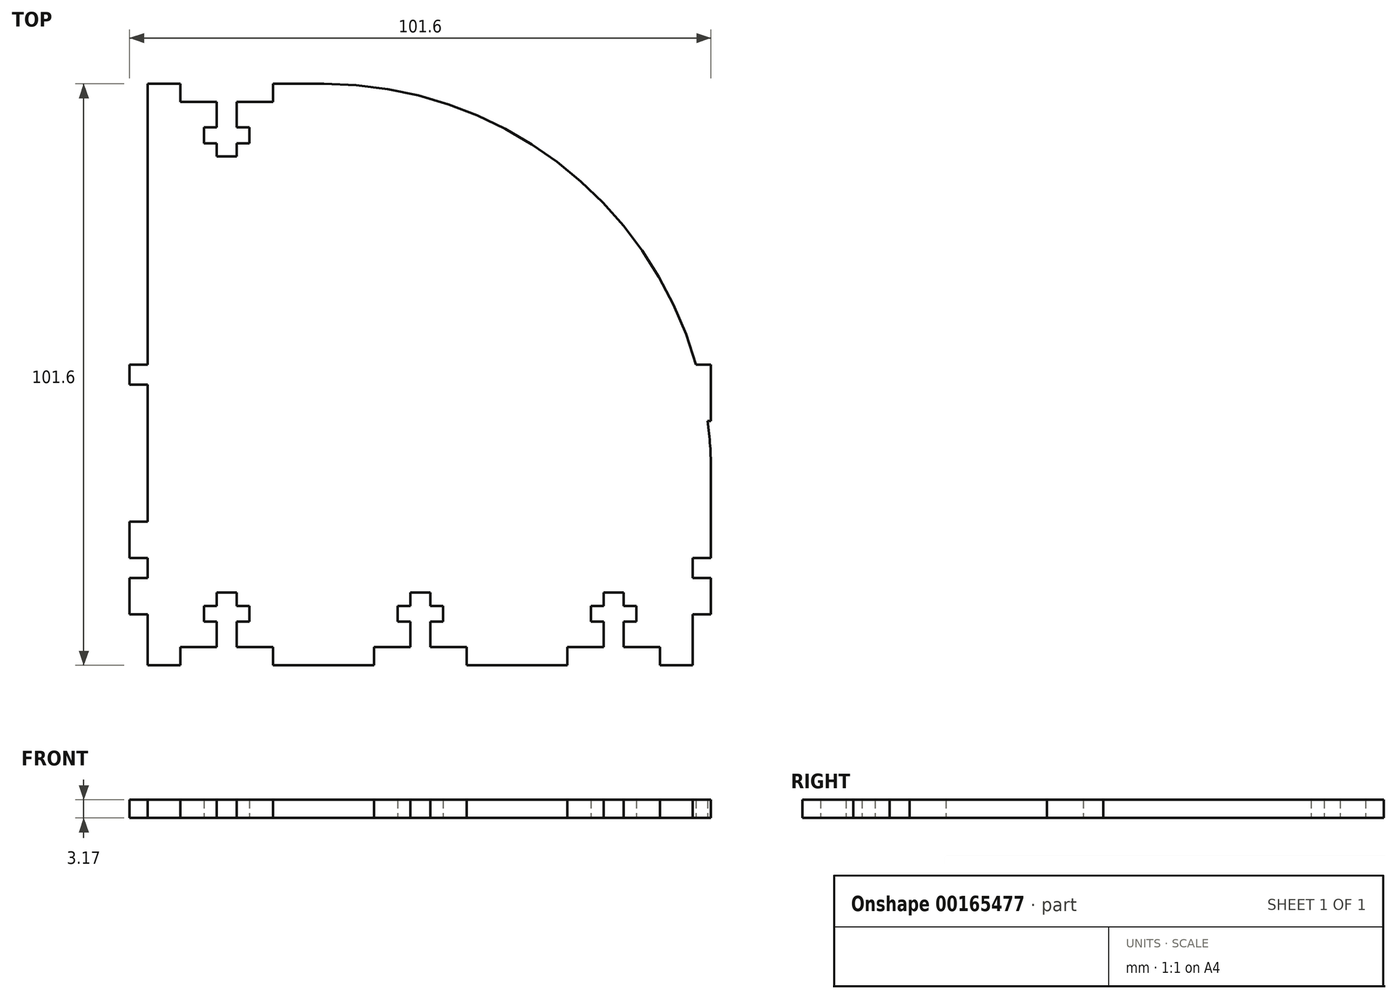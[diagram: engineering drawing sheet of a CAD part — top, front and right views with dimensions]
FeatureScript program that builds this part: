
annotation { "Feature Type Name" : "Feature", "Feature Type Description" : "" }
export const myFeature = defineFeature(function(context is Context, id is Id, definition is map)
    precondition{}
    {
        {
            var Q0;
            Q0=qCreatedBy(makeId("Top.planeOp"),FACE);
            var sketch = newSketch(context, id + "F0", { "sketchPlane" : qUnion([Q0])});
            skLineSegment(sketch, "E0.top", {"start": v(-48.14, 94.54) * mm, "end": v(53.46, 94.54) * mm});
            skLineSegment(sketch, "E0.left", {"start": v(-48.14, -7.06) * mm, "end": v(-48.14, 94.54) * mm});
            skLineSegment(sketch, "E0.right", {"start": v(53.46, -7.06) * mm, "end": v(53.46, 94.54) * mm});
            skLineSegment(sketch, "E1.bottom", {"start": v(-32.9, 94.54) * mm, "end": v(-29.4, 94.54) * mm});
            skLineSegment(sketch, "E1.top", {"start": v(-32.9, 81.84) * mm, "end": v(-29.4, 81.84) * mm});
            skLineSegment(sketch, "E1.left", {"start": v(-32.9, 94.54) * mm, "end": v(-32.9, 81.84) * mm});
            skLineSegment(sketch, "E1.right", {"start": v(-29.4, 94.54) * mm, "end": v(-29.4, 81.84) * mm});
            skLineSegment(sketch, "E2.bottom", {"start": v(-27.18, 84.14) * mm, "end": v(-35.11, 84.14) * mm});
            skLineSegment(sketch, "E2.top", {"start": v(-27.18, 86.92) * mm, "end": v(-35.11, 86.92) * mm});
            skLineSegment(sketch, "E2.left", {"start": v(-27.18, 84.14) * mm, "end": v(-27.18, 86.92) * mm});
            skLineSegment(sketch, "E2.right", {"start": v(-35.11, 84.14) * mm, "end": v(-35.11, 86.92) * mm});
            skLineSegment(sketch, "E3", {"start": v(-108, 43.74) * mm, "end": v(92.5, 43.74) * mm});
            skLineSegment(sketch, "E4.bottom", {"start": v(-39.25, 94.54) * mm, "end": v(-23.04, 94.54) * mm});
            skLineSegment(sketch, "E4.top", {"start": v(-39.25, 91.37) * mm, "end": v(-23.04, 91.37) * mm});
            skLineSegment(sketch, "E4.left", {"start": v(-39.25, 94.54) * mm, "end": v(-39.25, 91.37) * mm});
            skLineSegment(sketch, "E4.right", {"start": v(-23.04, 94.54) * mm, "end": v(-23.04, 91.37) * mm});
            skLineSegment(sketch, "E5.1.0.0", {"start": v(-5.44, 91.37) * mm, "end": v(10.76, 91.37) * mm});
            skLineSegment(sketch, "E5.1.0.1", {"start": v(4.41, 94.54) * mm, "end": v(4.41, 81.84) * mm});
            skLineSegment(sketch, "E5.1.0.2", {"start": v(0.9, 94.54) * mm, "end": v(0.9, 81.84) * mm});
            skLineSegment(sketch, "E5.1.0.3", {"start": v(-5.44, 94.54) * mm, "end": v(10.76, 94.54) * mm});
            skLineSegment(sketch, "E5.1.0.4", {"start": v(6.63, 86.92) * mm, "end": v(-1.3, 86.92) * mm});
            skLineSegment(sketch, "E5.1.0.6", {"start": v(-5.44, 94.54) * mm, "end": v(-5.44, 91.37) * mm});
            skLineSegment(sketch, "E5.1.0.7", {"start": v(0.9, 94.54) * mm, "end": v(4.41, 94.54) * mm});
            skLineSegment(sketch, "E5.1.0.8", {"start": v(10.76, 94.54) * mm, "end": v(10.76, 91.37) * mm});
            skLineSegment(sketch, "E5.1.0.9", {"start": v(0.9, 81.84) * mm, "end": v(4.41, 81.84) * mm});
            skLineSegment(sketch, "E5.1.0.10", {"start": v(6.63, 84.14) * mm, "end": v(6.63, 86.92) * mm});
            skLineSegment(sketch, "E5.1.0.11", {"start": v(6.63, 84.14) * mm, "end": v(-1.3, 84.14) * mm});
            skLineSegment(sketch, "E5.1.0.12", {"start": v(-1.3, 84.14) * mm, "end": v(-1.3, 86.92) * mm});
            skLineSegment(sketch, "E5.2.0.0", {"start": v(28.37, 91.37) * mm, "end": v(44.57, 91.37) * mm});
            skLineSegment(sketch, "E5.2.0.1", {"start": v(38.22, 94.54) * mm, "end": v(38.22, 81.84) * mm});
            skLineSegment(sketch, "E5.2.0.2", {"start": v(34.72, 94.54) * mm, "end": v(34.72, 81.84) * mm});
            skLineSegment(sketch, "E5.2.0.3", {"start": v(28.37, 94.54) * mm, "end": v(44.57, 94.54) * mm});
            skLineSegment(sketch, "E5.2.0.4", {"start": v(40.44, 86.92) * mm, "end": v(32.5, 86.92) * mm});
            skLineSegment(sketch, "E5.2.0.6", {"start": v(28.37, 94.54) * mm, "end": v(28.37, 91.37) * mm});
            skLineSegment(sketch, "E5.2.0.7", {"start": v(34.72, 94.54) * mm, "end": v(38.22, 94.54) * mm});
            skLineSegment(sketch, "E5.2.0.8", {"start": v(44.57, 94.54) * mm, "end": v(44.57, 91.37) * mm});
            skLineSegment(sketch, "E5.2.0.9", {"start": v(34.72, 81.84) * mm, "end": v(38.22, 81.84) * mm});
            skLineSegment(sketch, "E5.2.0.10", {"start": v(40.44, 84.14) * mm, "end": v(40.44, 86.92) * mm});
            skLineSegment(sketch, "E5.2.0.11", {"start": v(40.44, 84.14) * mm, "end": v(32.5, 84.14) * mm});
            skLineSegment(sketch, "E5.2.0.12", {"start": v(32.5, 84.14) * mm, "end": v(32.5, 86.92) * mm});
            skLineSegment(sketch, "E5.direction1", {"start": v(-32.9, 81.84) * mm, "end": v(0.9, 81.84) * mm, "construction": true});
            skLineSegment(sketch, "E6.MirrorCS", {"start": v(0.9, 5.64) * mm, "end": v(4.41, 5.64) * mm});
            skLineSegment(sketch, "E7.MirrorCS", {"start": v(-32.9, 5.64) * mm, "end": v(-29.4, 5.64) * mm});
            skLineSegment(sketch, "E8.MirrorCS", {"start": v(-23.04, -7.06) * mm, "end": v(-23.04, -3.88) * mm});
            skLineSegment(sketch, "E9.MirrorCS", {"start": v(-32.9, -7.06) * mm, "end": v(-29.4, -7.06) * mm});
            skLineSegment(sketch, "E10.MirrorCS", {"start": v(-35.11, 3.34) * mm, "end": v(-35.11, 0.56) * mm});
            skLineSegment(sketch, "E11.MirrorCS", {"start": v(-5.44, -7.06) * mm, "end": v(-5.44, -3.88) * mm});
            skLineSegment(sketch, "E12.MirrorCS", {"start": v(0.9, -7.06) * mm, "end": v(0.9, 5.64) * mm});
            skLineSegment(sketch, "E13.MirrorCS", {"start": v(-27.18, 3.34) * mm, "end": v(-27.18, 0.56) * mm});
            skLineSegment(sketch, "E14.MirrorCS", {"start": v(34.72, -7.06) * mm, "end": v(34.72, 5.64) * mm});
            skLineSegment(sketch, "E15.MirrorCS", {"start": v(0.9, -7.06) * mm, "end": v(4.41, -7.06) * mm});
            skLineSegment(sketch, "E16.MirrorCS", {"start": v(4.41, -7.06) * mm, "end": v(4.41, 5.64) * mm});
            skLineSegment(sketch, "E17.MirrorCS", {"start": v(40.44, 3.34) * mm, "end": v(40.44, 0.56) * mm});
            skLineSegment(sketch, "E18.MirrorCS", {"start": v(-39.25, -7.06) * mm, "end": v(-23.04, -7.06) * mm});
            skLineSegment(sketch, "E19.MirrorCS", {"start": v(-1.3, 3.34) * mm, "end": v(-1.3, 0.56) * mm});
            skLineSegment(sketch, "E20.MirrorCS", {"start": v(-5.44, -7.06) * mm, "end": v(10.76, -7.06) * mm});
            skLineSegment(sketch, "E21.MirrorCS", {"start": v(34.72, 5.64) * mm, "end": v(38.22, 5.64) * mm});
            skLineSegment(sketch, "E22.MirrorCS", {"start": v(28.37, -7.06) * mm, "end": v(28.37, -3.88) * mm});
            skLineSegment(sketch, "E23.MirrorCS", {"start": v(40.44, 3.34) * mm, "end": v(32.5, 3.34) * mm});
            skLineSegment(sketch, "E24.MirrorCS", {"start": v(28.37, -7.06) * mm, "end": v(44.57, -7.06) * mm});
            skLineSegment(sketch, "E25.MirrorCS", {"start": v(6.63, 3.34) * mm, "end": v(6.63, 0.56) * mm});
            skLineSegment(sketch, "E26.MirrorCS", {"start": v(10.76, -7.06) * mm, "end": v(10.76, -3.88) * mm});
            skLineSegment(sketch, "E27.MirrorCS", {"start": v(-32.9, -7.06) * mm, "end": v(-32.9, 5.64) * mm});
            skLineSegment(sketch, "E28.MirrorCS", {"start": v(-27.18, 3.34) * mm, "end": v(-35.11, 3.34) * mm});
            skLineSegment(sketch, "E29.MirrorCS", {"start": v(34.72, -7.06) * mm, "end": v(38.22, -7.06) * mm});
            skLineSegment(sketch, "E30.MirrorCS", {"start": v(44.57, -7.06) * mm, "end": v(44.57, -3.88) * mm});
            skLineSegment(sketch, "E31.MirrorCS", {"start": v(-39.25, -7.06) * mm, "end": v(-39.25, -3.88) * mm});
            skLineSegment(sketch, "E32.MirrorCS", {"start": v(32.5, 3.34) * mm, "end": v(32.5, 0.56) * mm});
            skLineSegment(sketch, "E33.MirrorCS", {"start": v(6.63, 3.34) * mm, "end": v(-1.3, 3.34) * mm});
            skLineSegment(sketch, "E34.MirrorCS", {"start": v(-29.4, -7.06) * mm, "end": v(-29.4, 5.64) * mm});
            skLineSegment(sketch, "E35.MirrorCS", {"start": v(38.22, -7.06) * mm, "end": v(38.22, 5.64) * mm});
            skLineSegment(sketch, "E36.MirrorCS", {"start": v(40.44, 0.56) * mm, "end": v(32.5, 0.56) * mm});
            skLineSegment(sketch, "E37.MirrorCS", {"start": v(-27.18, 0.56) * mm, "end": v(-35.11, 0.56) * mm});
            skLineSegment(sketch, "E38.MirrorCS", {"start": v(-32.9, 5.64) * mm, "end": v(0.9, 5.64) * mm, "construction": true});
            skLineSegment(sketch, "E39.MirrorCS", {"start": v(28.37, -3.88) * mm, "end": v(44.57, -3.88) * mm});
            skLineSegment(sketch, "E40.MirrorCS", {"start": v(-39.25, -3.88) * mm, "end": v(-23.04, -3.88) * mm});
            skLineSegment(sketch, "E41.MirrorCS", {"start": v(6.63, 0.56) * mm, "end": v(-1.3, 0.56) * mm});
            skLineSegment(sketch, "E42.MirrorCS", {"start": v(53.46, 94.54) * mm, "end": v(53.46, -7.06) * mm});
            skLineSegment(sketch, "E43.MirrorCS", {"start": v(-5.44, -3.88) * mm, "end": v(10.76, -3.88) * mm});
            skLineSegment(sketch, "E44.MirrorCS", {"start": v(-48.14, -7.06) * mm, "end": v(53.46, -7.06) * mm});
            skLineSegment(sketch, "E45.MirrorCS", {"start": v(-48.14, 94.54) * mm, "end": v(-48.14, -7.06) * mm});
            skLineSegment(sketch, "E46.bottom", {"start": v(-48.14, 94.54) * mm, "end": v(-44.96, 94.54) * mm});
            skLineSegment(sketch, "E46.top", {"start": v(-48.14, -7.06) * mm, "end": v(-44.96, -7.06) * mm});
            skLineSegment(sketch, "E46.right", {"start": v(-44.96, 94.54) * mm, "end": v(-44.96, -7.06) * mm});
            skLineSegment(sketch, "E47.bottom", {"start": v(53.46, -7.06) * mm, "end": v(50.29, -7.06) * mm});
            skLineSegment(sketch, "E47.top", {"start": v(53.46, 94.54) * mm, "end": v(50.29, 94.54) * mm});
            skLineSegment(sketch, "E47.right", {"start": v(50.29, -7.06) * mm, "end": v(50.29, 94.54) * mm});
            skLineSegment(sketch, "E48.bottom", {"start": v(-44.96, 1.83) * mm, "end": v(-48.14, 1.83) * mm});
            skLineSegment(sketch, "E48.top", {"start": v(-44.96, 8.18) * mm, "end": v(-48.14, 8.18) * mm});
            skLineSegment(sketch, "E48.left", {"start": v(-44.96, 1.83) * mm, "end": v(-44.96, 8.18) * mm});
            skLineSegment(sketch, "E48.right", {"start": v(-48.14, 1.83) * mm, "end": v(-48.14, 8.18) * mm});
            skLineSegment(sketch, "E49.top", {"start": v(-44.96, 11.69) * mm, "end": v(-48.14, 11.69) * mm});
            skLineSegment(sketch, "E49.left", {"start": v(-44.96, 8.18) * mm, "end": v(-44.96, 11.69) * mm});
            skLineSegment(sketch, "E49.right", {"start": v(-48.14, 8.18) * mm, "end": v(-48.14, 11.69) * mm});
            skLineSegment(sketch, "E50.top", {"start": v(-44.96, 18.04) * mm, "end": v(-48.14, 18.04) * mm});
            skLineSegment(sketch, "E50.left", {"start": v(-44.96, 11.69) * mm, "end": v(-44.96, 18.04) * mm});
            skLineSegment(sketch, "E50.right", {"start": v(-48.14, 11.69) * mm, "end": v(-48.14, 18.04) * mm});
            skLineSegment(sketch, "E51.0.1.0", {"start": v(-48.14, 41.99) * mm, "end": v(-48.14, 45.5) * mm});
            skLineSegment(sketch, "E51.0.1.1", {"start": v(-44.96, 35.64) * mm, "end": v(-44.96, 41.99) * mm});
            skLineSegment(sketch, "E51.0.1.2", {"start": v(-44.96, 35.64) * mm, "end": v(-48.14, 35.64) * mm});
            skLineSegment(sketch, "E51.0.1.3", {"start": v(-48.14, 45.5) * mm, "end": v(-48.14, 51.84) * mm});
            skLineSegment(sketch, "E51.0.1.4", {"start": v(-44.96, 41.99) * mm, "end": v(-44.96, 45.5) * mm});
            skLineSegment(sketch, "E51.0.1.5", {"start": v(-44.96, 45.5) * mm, "end": v(-48.14, 45.5) * mm});
            skLineSegment(sketch, "E51.0.1.6", {"start": v(-44.96, 45.5) * mm, "end": v(-44.96, 51.84) * mm});
            skLineSegment(sketch, "E51.0.1.7", {"start": v(-48.14, 35.64) * mm, "end": v(-48.14, 41.99) * mm});
            skLineSegment(sketch, "E51.0.1.8", {"start": v(-44.96, 41.99) * mm, "end": v(-48.14, 41.99) * mm});
            skLineSegment(sketch, "E51.0.1.9", {"start": v(-44.96, 51.84) * mm, "end": v(-48.14, 51.84) * mm});
            skLineSegment(sketch, "E51.0.1.10", {"start": v(-44.96, 41.99) * mm, "end": v(-48.14, 41.99) * mm});
            skLineSegment(sketch, "E51.0.1.11", {"start": v(-44.96, 45.5) * mm, "end": v(-48.14, 45.5) * mm});
            skLineSegment(sketch, "E51.0.2.0", {"start": v(-48.14, 75.8) * mm, "end": v(-48.14, 79.3) * mm});
            skLineSegment(sketch, "E51.0.2.1", {"start": v(-44.96, 69.45) * mm, "end": v(-44.96, 75.8) * mm});
            skLineSegment(sketch, "E51.0.2.2", {"start": v(-44.96, 69.45) * mm, "end": v(-48.14, 69.45) * mm});
            skLineSegment(sketch, "E51.0.2.3", {"start": v(-48.14, 79.3) * mm, "end": v(-48.14, 85.65) * mm});
            skLineSegment(sketch, "E51.0.2.4", {"start": v(-44.96, 75.8) * mm, "end": v(-44.96, 79.3) * mm});
            skLineSegment(sketch, "E51.0.2.5", {"start": v(-44.96, 79.3) * mm, "end": v(-48.14, 79.3) * mm});
            skLineSegment(sketch, "E51.0.2.6", {"start": v(-44.96, 79.3) * mm, "end": v(-44.96, 85.65) * mm});
            skLineSegment(sketch, "E51.0.2.7", {"start": v(-48.14, 69.45) * mm, "end": v(-48.14, 75.8) * mm});
            skLineSegment(sketch, "E51.0.2.8", {"start": v(-44.96, 75.8) * mm, "end": v(-48.14, 75.8) * mm});
            skLineSegment(sketch, "E51.0.2.9", {"start": v(-44.96, 85.65) * mm, "end": v(-48.14, 85.65) * mm});
            skLineSegment(sketch, "E51.0.2.10", {"start": v(-44.96, 75.8) * mm, "end": v(-48.14, 75.8) * mm});
            skLineSegment(sketch, "E51.0.2.11", {"start": v(-44.96, 79.3) * mm, "end": v(-48.14, 79.3) * mm});
            skLineSegment(sketch, "E51.direction1", {"start": v(-48.14, 1.83) * mm, "end": v(-22.74, 1.83) * mm, "construction": true});
            skLineSegment(sketch, "E51.direction2", {"start": v(-48.14, 1.83) * mm, "end": v(-48.14, 35.64) * mm, "construction": true});
            skLineSegment(sketch, "E52", {"start": v(2.66, 112.42) * mm, "end": v(2.66, 100.35) * mm});
            skLineSegment(sketch, "E53.MirrorCS", {"start": v(50.29, 75.8) * mm, "end": v(53.46, 75.8) * mm});
            skLineSegment(sketch, "E54.MirrorCS", {"start": v(50.29, 11.69) * mm, "end": v(53.46, 11.69) * mm});
            skLineSegment(sketch, "E55.MirrorCS", {"start": v(50.29, 79.3) * mm, "end": v(53.46, 79.3) * mm});
            skLineSegment(sketch, "E56.MirrorCS", {"start": v(50.29, 8.18) * mm, "end": v(53.46, 8.18) * mm});
            skLineSegment(sketch, "E57.MirrorCS", {"start": v(50.29, 45.5) * mm, "end": v(53.46, 45.5) * mm});
            skLineSegment(sketch, "E58.MirrorCS", {"start": v(50.29, 41.99) * mm, "end": v(53.46, 41.99) * mm});
            skLineSegment(sketch, "E59.MirrorCS", {"start": v(53.46, 75.8) * mm, "end": v(53.46, 79.3) * mm});
            skLineSegment(sketch, "E60.MirrorCS", {"start": v(53.46, 8.18) * mm, "end": v(53.46, 11.69) * mm});
            skLineSegment(sketch, "E61.MirrorCS", {"start": v(50.29, 41.99) * mm, "end": v(50.29, 45.5) * mm});
            skLineSegment(sketch, "E62.MirrorCS", {"start": v(50.29, 1.83) * mm, "end": v(53.46, 1.83) * mm});
            skLineSegment(sketch, "E63.MirrorCS", {"start": v(50.29, 8.18) * mm, "end": v(50.29, 11.69) * mm});
            skLineSegment(sketch, "E64.MirrorCS", {"start": v(53.46, 41.99) * mm, "end": v(53.46, 45.5) * mm});
            skLineSegment(sketch, "E65.MirrorCS", {"start": v(53.46, 1.83) * mm, "end": v(53.46, 8.18) * mm});
            skLineSegment(sketch, "E66.MirrorCS", {"start": v(50.29, 75.8) * mm, "end": v(50.29, 79.3) * mm});
            skLineSegment(sketch, "E67.MirrorCS", {"start": v(50.29, 35.64) * mm, "end": v(53.46, 35.64) * mm});
            skLineSegment(sketch, "E68.MirrorCS", {"start": v(53.46, 35.64) * mm, "end": v(53.46, 41.99) * mm});
            skLineSegment(sketch, "E69.MirrorCS", {"start": v(50.29, 18.04) * mm, "end": v(53.46, 18.04) * mm});
            skLineSegment(sketch, "E70.MirrorCS", {"start": v(50.29, 69.45) * mm, "end": v(50.29, 75.8) * mm});
            skLineSegment(sketch, "E71.MirrorCS", {"start": v(50.29, 11.69) * mm, "end": v(50.29, 18.04) * mm});
            skLineSegment(sketch, "E72.MirrorCS", {"start": v(53.46, 45.5) * mm, "end": v(53.46, 51.84) * mm});
            skLineSegment(sketch, "E73.MirrorCS", {"start": v(53.46, 69.45) * mm, "end": v(53.46, 75.8) * mm});
            skLineSegment(sketch, "E74.MirrorCS", {"start": v(50.29, 79.3) * mm, "end": v(50.29, 85.65) * mm});
            skLineSegment(sketch, "E75.MirrorCS", {"start": v(50.29, 69.45) * mm, "end": v(53.46, 69.45) * mm});
            skLineSegment(sketch, "E76.MirrorCS", {"start": v(50.29, 35.64) * mm, "end": v(50.29, 41.99) * mm});
            skLineSegment(sketch, "E77.MirrorCS", {"start": v(50.29, 51.84) * mm, "end": v(53.46, 51.84) * mm});
            skLineSegment(sketch, "E78.MirrorCS", {"start": v(50.29, 1.83) * mm, "end": v(50.29, 8.18) * mm});
            skLineSegment(sketch, "E79.MirrorCS", {"start": v(50.29, 45.5) * mm, "end": v(50.29, 51.84) * mm});
            skLineSegment(sketch, "E80.MirrorCS", {"start": v(53.46, 11.69) * mm, "end": v(53.46, 18.04) * mm});
            skLineSegment(sketch, "E81.MirrorCS", {"start": v(53.46, 79.3) * mm, "end": v(53.46, 85.65) * mm});
            skLineSegment(sketch, "E82.MirrorCS", {"start": v(50.29, 85.65) * mm, "end": v(53.46, 85.65) * mm});
            skLineSegment(sketch, "E83.MirrorCS", {"start": v(53.46, 1.83) * mm, "end": v(53.46, 35.64) * mm, "construction": true});
            skLineSegment(sketch, "E84.MirrorCS", {"start": v(50.29, 94.54) * mm, "end": v(50.29, -7.06) * mm});
            skArc(sketch, "E85", {"start": v(53.46, 26.93) * mm, "mid": v(33.66, 74.74) * mm, "end": v(-14.15, 94.54) * mm});
            skLineSegment(sketch, "E86.bottom", {"start": v(53.46, 26.93) * mm, "end": v(50.29, 26.93) * mm});
            skLineSegment(sketch, "E86.top", {"start": v(53.46, 18.04) * mm, "end": v(50.29, 18.04) * mm});
            skLineSegment(sketch, "E86.left", {"start": v(53.46, 26.93) * mm, "end": v(53.46, 18.04) * mm});
            skLineSegment(sketch, "E86.right", {"start": v(50.29, 26.93) * mm, "end": v(50.29, 18.04) * mm});
            skSolve(sketch);
        }
        {
            var Q0;
            {var subQ0=sQuery(id+"F0.wireOp",EDGE,"E84.MirrorCS");var subQ1=sQuery(id+"F0.wireOp",EDGE,"E58.MirrorCS");var subQ2=makeQuery(id+"F0.imprint","INTERSECT",VERTEX,{"derivedFrom":[subQ1,subQ0]});Q0=makeQuery(id+"F0.imprint","IMPRINT",FACE,{"disambiguationData":[TD([[makeQuery(id+"F0.imprint","IMPRINT",EDGE,{"disambiguationData":[TD([[subQ2,-1.0]])],"derivedFrom":subQ1}),-1.0]])]});}
            var Q1;
            {var subQ31=sQuery(id+"F0.wireOp",EDGE,"E1.top");Q1=makeQuery(id+"F0.imprint","IMPRINT",FACE,{"disambiguationData":[TD([[makeQuery(id+"F0.imprint","IMPRINT",EDGE,{"derivedFrom":subQ31}),-1.0]])]});}
            var Q2;
            {var subQ50=sQuery(id+"F0.wireOp",EDGE,"E6.MirrorCS");Q2=makeQuery(id+"F0.imprint","IMPRINT",FACE,{"disambiguationData":[TD([[makeQuery(id+"F0.imprint","IMPRINT",EDGE,{"derivedFrom":subQ50}),1.0]])]});}
            var Q3;
            Q3=makeQuery(id+"F0.imprint","IMPRINT",FACE,{"disambiguationData":[TD([[makeQuery(id+"F0.imprint","IMPRINT",EDGE,{"derivedFrom":sQuery(id+"F0.wireOp",EDGE,"E51.0.1.3")}),-1.0]])]});
            var Q4;
            Q4=makeQuery(id+"F0.imprint","IMPRINT",FACE,{"disambiguationData":[TD([[makeQuery(id+"F0.imprint","IMPRINT",EDGE,{"derivedFrom":sQuery(id+"F0.wireOp",EDGE,"E51.0.2.1")}),1.0]])]});
            var Q5;
            Q5=makeQuery(id+"F0.imprint","IMPRINT",FACE,{"disambiguationData":[TD([[makeQuery(id+"F0.imprint","IMPRINT",EDGE,{"derivedFrom":sQuery(id+"F0.wireOp",EDGE,"E51.0.2.3")}),-1.0]])]});
            var Q6;
            Q6=makeQuery(id+"F0.imprint","IMPRINT",FACE,{"disambiguationData":[TD([[makeQuery(id+"F0.imprint","IMPRINT",EDGE,{"derivedFrom":sQuery(id+"F0.wireOp",EDGE,"E51.0.1.1")}),1.0]])]});
            var Q7;
            Q7=makeQuery(id+"F0.imprint","IMPRINT",FACE,{"disambiguationData":[TD([[makeQuery(id+"F0.imprint","IMPRINT",EDGE,{"derivedFrom":sQuery(id+"F0.wireOp",EDGE,"E49.top")}),-1.0]])]});
            var Q8;
            Q8=makeQuery(id+"F0.imprint","IMPRINT",FACE,{"disambiguationData":[TD([[makeQuery(id+"F0.imprint","IMPRINT",EDGE,{"derivedFrom":sQuery(id+"F0.wireOp",EDGE,"E48.bottom")}),-1.0]])]});
            var Q9;
            {var subQ0=sQuery(id+"F0.wireOp",EDGE,"E62.MirrorCS");Q9=makeQuery(id+"F0.imprint","IMPRINT",FACE,{"disambiguationData":[TD([[makeQuery(id+"F0.imprint","IMPRINT",EDGE,{"derivedFrom":subQ0}),1.0]])]});}
            var Q10;
            {var subQ0=sQuery(id+"F0.wireOp",EDGE,"E54.MirrorCS");Q10=makeQuery(id+"F0.imprint","IMPRINT",FACE,{"disambiguationData":[TD([[makeQuery(id+"F0.imprint","IMPRINT",EDGE,{"derivedFrom":subQ0}),1.0]])]});}
            var Q11;
            {var subQ0=sQuery(id+"F0.wireOp",EDGE,"E84.MirrorCS");var subQ1=sQuery(id+"F0.wireOp",EDGE,"E57.MirrorCS");var subQ2=makeQuery(id+"F0.imprint","INTERSECT",VERTEX,{"derivedFrom":[subQ1,subQ0]});Q11=makeQuery(id+"F0.imprint","IMPRINT",FACE,{"disambiguationData":[TD([[makeQuery(id+"F0.imprint","IMPRINT",EDGE,{"disambiguationData":[TD([[subQ2,-1.0]])],"derivedFrom":subQ1}),1.0]])]});}
            var Q12;
            {var subQ0=sQuery(id+"F0.wireOp",EDGE,"E5.1.0.6");var subQ1=sQuery(id+"F0.wireOp",EDGE,"E5.1.0.0");var subQ2=makeQuery(id+"F0.imprint","INTERSECT",VERTEX,{"derivedFrom":[subQ1,subQ0]});Q12=makeQuery(id+"F0.imprint","IMPRINT",FACE,{"disambiguationData":[TD([[makeQuery(id+"F0.imprint","IMPRINT",EDGE,{"disambiguationData":[TD([[subQ2,-1.0]])],"derivedFrom":subQ1}),1.0]])]});}
            var Q13;
            {var subQ0=sQuery(id+"F0.wireOp",EDGE,"E5.1.0.2");var subQ1=sQuery(id+"F0.wireOp",EDGE,"E5.1.0.0");var subQ2=makeQuery(id+"F0.imprint","INTERSECT",VERTEX,{"derivedFrom":[subQ1,subQ0]});Q13=makeQuery(id+"F0.imprint","IMPRINT",FACE,{"disambiguationData":[TD([[makeQuery(id+"F0.imprint","IMPRINT",EDGE,{"disambiguationData":[TD([[subQ2,-1.0]])],"derivedFrom":subQ1}),1.0]])]});}
            var Q14;
            {var subQ0=sQuery(id+"F0.wireOp",EDGE,"E5.1.0.2");var subQ1=sQuery(id+"F0.wireOp",EDGE,"E5.1.0.0");var subQ2=makeQuery(id+"F0.imprint","INTERSECT",VERTEX,{"derivedFrom":[subQ1,subQ0]});Q14=makeQuery(id+"F0.imprint","IMPRINT",FACE,{"disambiguationData":[TD([[makeQuery(id+"F0.imprint","IMPRINT",EDGE,{"disambiguationData":[TD([[subQ2,-1.0]])],"derivedFrom":subQ1}),-1.0]])]});}
            var Q15;
            {var subQ0=sQuery(id+"F0.wireOp",EDGE,"E5.1.0.4");var subQ1=sQuery(id+"F0.wireOp",EDGE,"E5.1.0.1");var subQ2=makeQuery(id+"F0.imprint","INTERSECT",VERTEX,{"derivedFrom":[subQ1,subQ0]});Q15=makeQuery(id+"F0.imprint","IMPRINT",FACE,{"disambiguationData":[TD([[makeQuery(id+"F0.imprint","IMPRINT",EDGE,{"disambiguationData":[TD([[subQ2,-1.0]])],"derivedFrom":subQ1}),-1.0]])]});}
            var Q16;
            {var subQ0=sQuery(id+"F0.wireOp",EDGE,"E5.1.0.9");Q16=makeQuery(id+"F0.imprint","IMPRINT",FACE,{"disambiguationData":[TD([[makeQuery(id+"F0.imprint","IMPRINT",EDGE,{"derivedFrom":subQ0}),1.0]])]});}
            var Q17;
            {var subQ5=sQuery(id+"F0.wireOp",EDGE,"E5.1.0.12");Q17=makeQuery(id+"F0.imprint","IMPRINT",FACE,{"disambiguationData":[TD([[makeQuery(id+"F0.imprint","IMPRINT",EDGE,{"derivedFrom":subQ5}),-1.0]])]});}
            var Q18;
            {var subQ5=sQuery(id+"F0.wireOp",EDGE,"E5.1.0.10");Q18=makeQuery(id+"F0.imprint","IMPRINT",FACE,{"disambiguationData":[TD([[makeQuery(id+"F0.imprint","IMPRINT",EDGE,{"derivedFrom":subQ5}),1.0]])]});}
            var Q19;
            {var subQ0=sQuery(id+"F0.wireOp",EDGE,"E84.MirrorCS");var subQ1=sQuery(id+"F0.wireOp",EDGE,"E3");var subQ2=makeQuery(id+"F0.imprint","INTERSECT",VERTEX,{"derivedFrom":[subQ1,subQ0]});Q19=makeQuery(id+"F0.imprint","IMPRINT",FACE,{"disambiguationData":[TD([[makeQuery(id+"F0.imprint","IMPRINT",EDGE,{"disambiguationData":[TD([[subQ2,-1.0]])],"derivedFrom":subQ1}),-1.0]])]});}
            var Q20;
            {var subQ0=sQuery(id+"F0.wireOp",EDGE,"E84.MirrorCS");var subQ1=sQuery(id+"F0.wireOp",EDGE,"E3");var subQ2=makeQuery(id+"F0.imprint","INTERSECT",VERTEX,{"derivedFrom":[subQ1,subQ0]});Q20=makeQuery(id+"F0.imprint","IMPRINT",FACE,{"disambiguationData":[TD([[makeQuery(id+"F0.imprint","IMPRINT",EDGE,{"disambiguationData":[TD([[subQ2,-1.0]])],"derivedFrom":subQ1}),1.0]])]});}
            var Q21;
            {var subQ3=sQuery(id+"F0.wireOp",EDGE,"E69.MirrorCS");Q21=makeQuery(id+"F0.imprint","IMPRINT",FACE,{"disambiguationData":[TD([[makeQuery(id+"F0.imprint","IMPRINT",EDGE,{"derivedFrom":subQ3}),1.0]])]});}
            var Q22;
            {var subQ0=sQuery(id+"F0.wireOp",EDGE,"E5.1.0.1");var subQ1=sQuery(id+"F0.wireOp",EDGE,"E5.1.0.0");var subQ2=makeQuery(id+"F0.imprint","INTERSECT",VERTEX,{"derivedFrom":[subQ1,subQ0]});Q22=makeQuery(id+"F0.imprint","IMPRINT",FACE,{"disambiguationData":[TD([[makeQuery(id+"F0.imprint","IMPRINT",EDGE,{"disambiguationData":[TD([[subQ2,-1.0]])],"derivedFrom":subQ1}),1.0]])]});}
            var Q23;
            {var subQ5=sQuery(id+"F0.wireOp",EDGE,"E86.bottom");Q23=makeQuery(id+"F0.imprint","IMPRINT",FACE,{"disambiguationData":[TD([[makeQuery(id+"F0.imprint","IMPRINT",EDGE,{"derivedFrom":subQ5}),-1.0]])]});}
            extrude(context, id + "F1", {"entities" : qUnion([Q0, Q1, Q2, Q3, Q4, Q5, Q6, Q7, Q8, Q9, Q10, Q11, Q12, Q13, Q14, Q15, Q16, Q17, Q18, Q19, Q20, Q21, Q22, Q23]), "depth" : 3.17 * mm});
        }
    });
